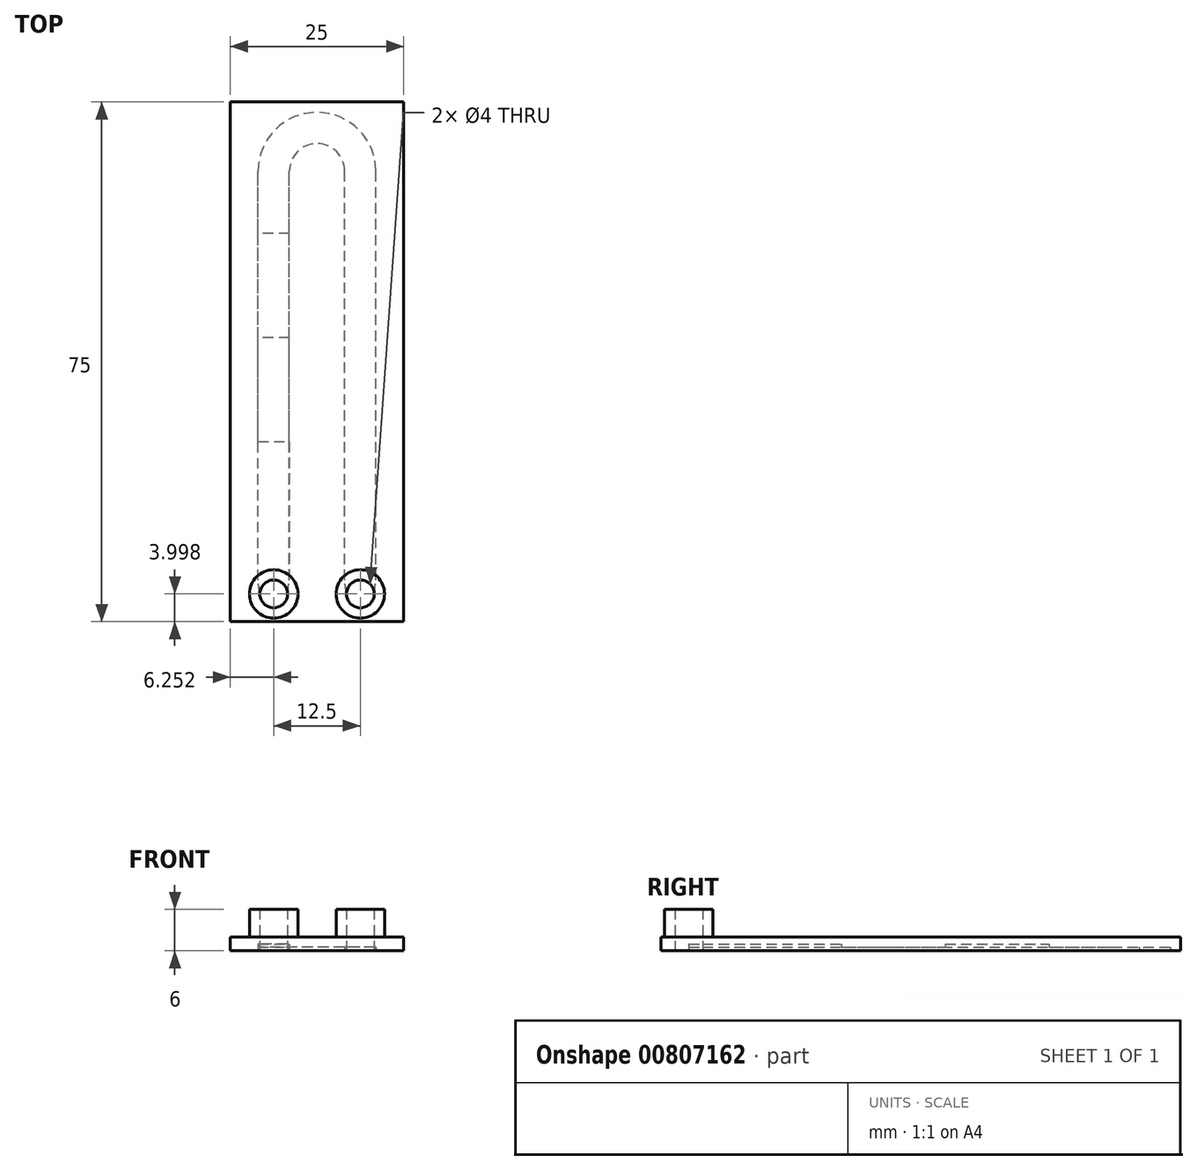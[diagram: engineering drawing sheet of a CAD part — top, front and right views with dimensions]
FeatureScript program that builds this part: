
annotation { "Feature Type Name" : "Feature", "Feature Type Description" : "" }
export const myFeature = defineFeature(function(context is Context, id is Id, definition is map)
    precondition{}
    {
        {
            var Q0;
            Q0=qCreatedBy(makeId("Top.planeOp"),FACE);
            var sketch = newSketch(context, id + "F0", { "sketchPlane" : qUnion([Q0])});
            skLineSegment(sketch, "E0.bottom", {"start": v(-44.29, 25.1) * mm, "end": v(-19.29, 25.1) * mm});
            skLineSegment(sketch, "E0.top", {"start": v(-44.29, -49.9) * mm, "end": v(-19.29, -49.9) * mm});
            skLineSegment(sketch, "E0.left", {"start": v(-44.29, 25.1) * mm, "end": v(-44.29, -49.9) * mm});
            skLineSegment(sketch, "E0.right", {"start": v(-19.29, 25.1) * mm, "end": v(-19.29, -49.9) * mm});
            skPoint(sketch, "E1", {"position": v(-31.79, -49.9) * mm});
            skPoint(sketch, "E2", {"position": v(-19.29, -12.4) * mm});
            skPoint(sketch, "E3", {"position": v(-44.29, -12.4) * mm});
            skPoint(sketch, "E4", {"position": v(-31.79, 25.1) * mm});
            skPoint(sketch, "E5", {"position": v(-31.79, -12.4) * mm});
            skPoint(sketch, "E6", {"position": v(-25.54, -49.9) * mm});
            skPoint(sketch, "E7", {"position": v(-38.04, -49.9) * mm});
            skPoint(sketch, "E8", {"position": v(-25.54, -43.64) * mm});
            skPoint(sketch, "E9", {"position": v(-38.04, -43.64) * mm});
            skSolve(sketch);
        }
        {
            var Q0;
            Q0=makeQuery(id+"F0.imprint","IMPRINT",FACE,{"disambiguationData":[TD([[makeQuery(id+"F0.imprint","IMPRINT",EDGE,{"derivedFrom":sQuery(id+"F0.wireOp",EDGE,"E0.bottom")}),-1.0]])]});
            var sketch = newSketch(context, id + "F1", { "sketchPlane" : qUnion([Q0])});
            skPoint(sketch, "E10", {"position": v(-25.54, -45.9) * mm});
            skPoint(sketch, "E11", {"position": v(-38.04, -45.9) * mm});
            skPoint(sketch, "E12", {"position": v(-25.54, 23.1) * mm});
            skPoint(sketch, "E13", {"position": v(-38.04, 23.1) * mm});
            skPoint(sketch, "E14", {"position": v(-31.79, 15.1) * mm});
            skCircle(sketch, "E15", {"center": v(-25.54, -45.9) * mm, "radius": 2 * mm});
            skCircle(sketch, "E16", {"center": v(-38.04, -45.9) * mm, "radius": 2 * mm});
            skPoint(sketch, "E17", {"position": v(-23.54, -45.9) * mm});
            skPoint(sketch, "E18", {"position": v(-27.54, -45.9) * mm});
            skPoint(sketch, "E19", {"position": v(-36.04, -45.9) * mm});
            skPoint(sketch, "E20", {"position": v(-40.04, -45.9) * mm});
            skPoint(sketch, "E21", {"position": v(-38.04, -43.9) * mm});
            skPoint(sketch, "E22", {"position": v(-35.79, -43.9) * mm});
            skPoint(sketch, "E23", {"position": v(-40.29, -43.9) * mm});
            skPoint(sketch, "E24", {"position": v(-27.79, -43.9) * mm});
            skPoint(sketch, "E25", {"position": v(-25.54, -43.9) * mm});
            skPoint(sketch, "E26", {"position": v(-23.29, -43.9) * mm});
            skPoint(sketch, "E27", {"position": v(-35.79, 15.1) * mm});
            skPoint(sketch, "E28", {"position": v(-40.29, 15.1) * mm});
            skPoint(sketch, "E29", {"position": v(-27.79, 15.1) * mm});
            skPoint(sketch, "E30", {"position": v(-23.29, 15.1) * mm});
            skLineSegment(sketch, "E31", {"start": v(-40.04, -45.9) * mm, "end": v(-40.29, -43.9) * mm});
            skLineSegment(sketch, "E32", {"start": v(-36.04, -45.9) * mm, "end": v(-35.79, -43.9) * mm});
            skLineSegment(sketch, "E33", {"start": v(-27.54, -45.9) * mm, "end": v(-27.79, -43.9) * mm});
            skLineSegment(sketch, "E34", {"start": v(-23.54, -45.9) * mm, "end": v(-23.29, -43.9) * mm});
            skLineSegment(sketch, "E35", {"start": v(-40.29, -43.9) * mm, "end": v(-40.29, 15.1) * mm});
            skLineSegment(sketch, "E36", {"start": v(-35.79, -43.9) * mm, "end": v(-35.79, 15.1) * mm});
            skLineSegment(sketch, "E37", {"start": v(-27.79, -43.9) * mm, "end": v(-27.79, 15.1) * mm});
            skLineSegment(sketch, "E38", {"start": v(-23.29, -43.9) * mm, "end": v(-23.29, 15.1) * mm});
            skArc(sketch, "E39", {"start": v(-35.79, 15.1) * mm, "mid": v(-31.79, 19.1) * mm, "end": v(-27.79, 15.1) * mm});
            skArc(sketch, "E40", {"start": v(-40.29, 15.1) * mm, "mid": v(-31.79, 23.6) * mm, "end": v(-23.29, 15.1) * mm});
            skPoint(sketch, "E41", {"position": v(-38.04, -43.64) * mm});
            skPoint(sketch, "E42", {"position": v(-23.29, 5.1) * mm});
            skPoint(sketch, "E43", {"position": v(-27.79, 5.1) * mm});
            skPoint(sketch, "E44", {"position": v(-35.79, 5.1) * mm});
            skPoint(sketch, "E45", {"position": v(-40.29, 5.1) * mm});
            skSolve(sketch);
        }
        {
            var Q0;
            Q0=qCreatedBy(makeId("Top.planeOp"),FACE);
            var sketch = newSketch(context, id + "F2", { "sketchPlane" : qUnion([Q0])});
            skPoint(sketch, "E46", {"position": v(-38.04, -45.9) * mm});
            skPoint(sketch, "E47", {"position": v(-25.54, -45.9) * mm});
            skSolve(sketch);
        }
        {
            var Q0;
            Q0=qSketchRegion(id+"F0",true);
            extrude(context, id + "F3", {"entities" : qUnion([Q0]), "depth" : 2 * mm, "offsetDistance" : 25 * mm});
        }
        {
            var Q0;
            Q0=qSketchRegion(id+"F1",true);
            extrude(context, id + "F4", {"entities" : qUnion([Q0]), "operationType" : NewBodyOperationType.REMOVE, "depth" : 0.5 * mm, "offsetDistance" : 25 * mm});
        }
        {
            var Q0;
            Q0=makeQuery(id+"F3.opExtrude","CAP_FACE",FACE,{"disambiguationData":[OSD([sQuery(id+"F0.wireOp",EDGE,"E0.bottom"),sQuery(id+"F0.wireOp",EDGE,"E0.top"),sQuery(id+"F0.wireOp",EDGE,"E0.left"),sQuery(id+"F0.wireOp",EDGE,"E0.right")])],"isStart":false});
            var sketch = newSketch(context, id + "F5", { "sketchPlane" : qUnion([Q0])});
            skPoint(sketch, "E48", {"position": v(-38.04, -45.9) * mm});
            skPoint(sketch, "E49", {"position": v(-25.54, -45.9) * mm});
            skSolve(sketch);
        }
        {
            var Q0;
            Q0=makeQuery(id+"F5.imprint","IMPRINT",FACE,{"disambiguationData":[TD([[makeQuery(id+"F5.imprint","IMPRINT",EDGE,{"derivedFrom":makeQuery(id+"F3.opExtrude","CAP_EDGE",EDGE,{"disambiguationData":[OSD([sQuery(id+"F0.wireOp",EDGE,"E0.bottom")])],"isStart":false})}),-1.0]])]});
            var sketch = newSketch(context, id + "F6", { "sketchPlane" : qUnion([Q0])});
            skPoint(sketch, "E50", {"position": v(-38.04, -45.9) * mm});
            skPoint(sketch, "E51", {"position": v(-25.54, -45.9) * mm});
            skCircle(sketch, "E52", {"center": v(-38.04, -45.9) * mm, "radius": 2 * mm});
            skCircle(sketch, "E53", {"center": v(-38.04, -45.9) * mm, "radius": 3.5 * mm});
            skCircle(sketch, "E54", {"center": v(-25.54, -45.9) * mm, "radius": 2 * mm});
            skCircle(sketch, "E55", {"center": v(-25.54, -45.9) * mm, "radius": 3.5 * mm});
            skSolve(sketch);
        }
        {
            var Q0;
            Q0 = qSketchRegion(id + "F6", true);
            extrude(context, id + "F7", {"entities" : qUnion([Q0]), "operationType" : NewBodyOperationType.ADD, "depth" : 4 * mm, "offsetDistance" : 25 * mm});
        }
        {
            var Q0;
            Q0=makeQuery(id+"F6.imprint","IMPRINT",FACE,{"disambiguationData":[TD([[makeQuery(id+"F6.imprint","IMPRINT",EDGE,{"derivedFrom":sQuery(id+"F6.wireOp",EDGE,"E54")}),1.0]])]});
            var Q1;
            Q1=makeQuery(id+"F6.imprint","IMPRINT",FACE,{"disambiguationData":[TD([[makeQuery(id+"F6.imprint","IMPRINT",EDGE,{"derivedFrom":sQuery(id+"F6.wireOp",EDGE,"E52")}),1.0]])]});
            extrude(context, id + "F8", {"entities" : qUnion([Q0, Q1]), "operationType" : NewBodyOperationType.REMOVE, "oppositeDirection" : true, "depth" : 1 * mm, "offsetDistance" : 25 * mm});
        }
        {
            var Q0;
            Q0=makeQuery(id+"F0.imprint","IMPRINT",FACE,{"disambiguationData":[TD([[makeQuery(id+"F0.imprint","IMPRINT",EDGE,{"derivedFrom":sQuery(id+"F0.wireOp",EDGE,"E0.bottom")}),-1.0]])]});
            var sketch = newSketch(context, id + "F9", { "sketchPlane" : qUnion([Q0])});
            skPoint(sketch, "E56", {"position": v(-31.74, -49.93) * mm});
            skPoint(sketch, "E57", {"position": v(-38.04, -45.9) * mm});
            skPoint(sketch, "E58", {"position": v(-38.04, -43.9) * mm});
            skPoint(sketch, "E59", {"position": v(-36.04, -45.9) * mm});
            skPoint(sketch, "E60", {"position": v(-40.04, -45.9) * mm});
            skPoint(sketch, "E61", {"position": v(-40.29, -43.9) * mm});
            skPoint(sketch, "E62", {"position": v(-35.79, -43.9) * mm});
            skArc(sketch, "E63", {"start": v(-40.04, -45.9) * mm, "mid": v(-38.04, -47.9) * mm, "end": v(-36.04, -45.9) * mm});
            skLineSegment(sketch, "E64", {"start": v(-40.04, -45.9) * mm, "end": v(-40.29, -43.9) * mm});
            skLineSegment(sketch, "E65", {"start": v(-36.04, -45.9) * mm, "end": v(-35.79, -43.9) * mm});
            skLineSegment(sketch, "E66", {"start": v(-40.29, -43.9) * mm, "end": v(-40.29, -23.9) * mm});
            skLineSegment(sketch, "E67", {"start": v(-35.79, -23.9) * mm, "end": v(-35.79, -43.9) * mm});
            skLineSegment(sketch, "E68", {"start": v(-35.79, -23.9) * mm, "end": v(-40.29, -23.9) * mm});
            skPoint(sketch, "E69", {"position": v(-40.29, -23.9) * mm});
            skPoint(sketch, "E70", {"position": v(-40.29, -8.9) * mm});
            skPoint(sketch, "E71", {"position": v(-35.79, -8.9) * mm});
            skLineSegment(sketch, "E72.bottom", {"start": v(-40.29, -8.9) * mm, "end": v(-35.79, -8.9) * mm});
            skLineSegment(sketch, "E72.left", {"start": v(-40.29, -8.9) * mm, "end": v(-40.29, 6.1) * mm});
            skLineSegment(sketch, "E72.right", {"start": v(-35.79, -8.9) * mm, "end": v(-35.79, 6.1) * mm});
            skPoint(sketch, "E73", {"position": v(-35.79, 15.1) * mm});
            skLineSegment(sketch, "E74", {"start": v(-40.29, 6.1) * mm, "end": v(-35.79, 6.1) * mm});
            skLineSegment(sketch, "E75", {"start": v(-35.79, 15.1) * mm, "end": v(-40.29, 15.1) * mm});
            skSolve(sketch);
        }
        {
            var Q0;
            Q0 = qSketchRegion(id + "F9", true);
            extrude(context, id + "F10", {"entities" : qUnion([Q0]), "operationType" : NewBodyOperationType.REMOVE, "depth" : 1 * mm, "offsetDistance" : 25 * mm});
        }
        {
            var Q0;
            Q0 = qSketchRegion(id + "F2", true);
            var Q1;
            Q1=makeQuery(id+"F6.imprint","IMPRINT",FACE,{"disambiguationData":[TD([[makeQuery(id+"F6.imprint","IMPRINT",EDGE,{"derivedFrom":sQuery(id+"F6.wireOp",EDGE,"E54")}),1.0]])]});
            var Q2;
            Q2=makeQuery(id+"F6.imprint","IMPRINT",FACE,{"disambiguationData":[TD([[makeQuery(id+"F6.imprint","IMPRINT",EDGE,{"derivedFrom":sQuery(id+"F6.wireOp",EDGE,"E52")}),1.0]])]});
            extrude(context, id + "F11", {"entities" : qUnion([Q0, Q1, Q2]), "operationType" : NewBodyOperationType.REMOVE, "oppositeDirection" : true, "depth" : 2 * mm, "offsetDistance" : 25 * mm});
        }
    });
